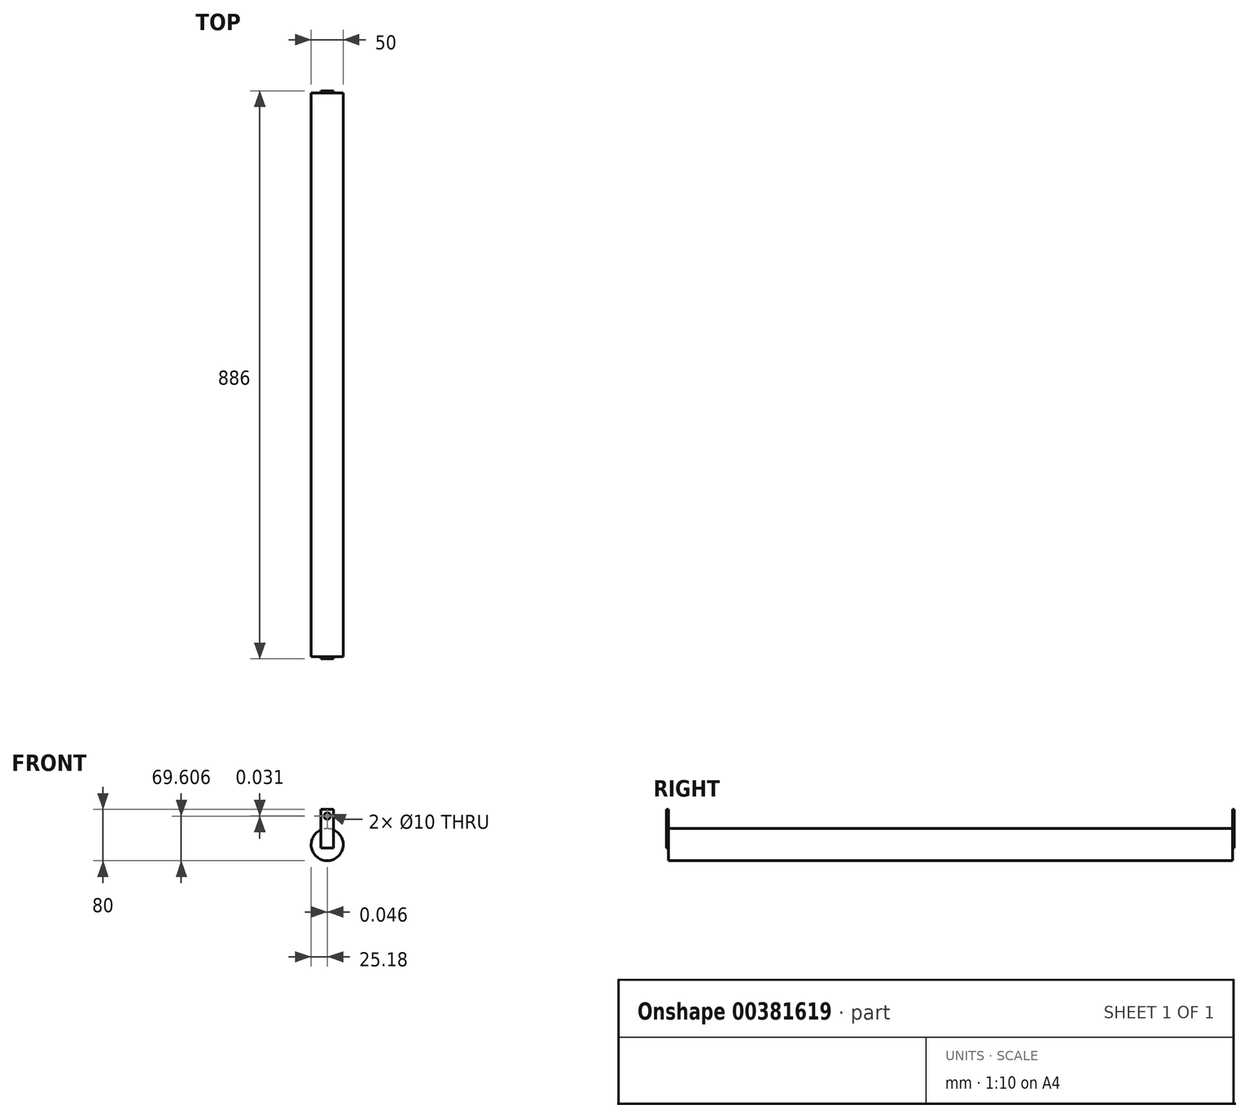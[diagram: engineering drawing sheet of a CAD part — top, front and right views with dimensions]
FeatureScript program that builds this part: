
annotation { "Feature Type Name" : "Feature", "Feature Type Description" : "" }
export const myFeature = defineFeature(function(context is Context, id is Id, definition is map)
    precondition{}
    {
        {
            var Q0;
            Q0=qCreatedBy(makeId("Front.planeOp"),FACE);
            var sketch = newSketch(context, id + "F0", { "sketchPlane" : qUnion([Q0])});
            skCircle(sketch, "E0", {"center": v(0, 0) * mm, "radius": 25 * mm});
            skLineSegment(sketch, "E1", {"start": v(-44.66, 25) * mm, "end": v(49.89, 25) * mm, "construction": true});
            skSolve(sketch);
        }
        {
            var Q0;
            Q0=makeQuery(id+"F0.imprint","IMPRINT",FACE,{"disambiguationData":[TD([[makeQuery(id+"F0.imprint","IMPRINT",EDGE,{"derivedFrom":sQuery(id+"F0.wireOp",EDGE,"E0")}),1.0]])]});
            extrude(context, id + "F1", {"entities" : qUnion([Q0]), "depth" : 880 * mm});
        }
        {
            var Q0;
            Q0=makeQuery(id+"F1.opExtrude","CAP_FACE",FACE,{"disambiguationData":[OSD([sQuery(id+"F0.wireOp",EDGE,"E0")])],"isStart":false});
            var sketch = newSketch(context, id + "F2", { "sketchPlane" : qUnion([Q0])});
            skLineSegment(sketch, "E2.bottom", {"start": v(-10, 55) * mm, "end": v(10, 55) * mm});
            skLineSegment(sketch, "E2.top", {"start": v(-10, -5) * mm, "end": v(10, -5) * mm});
            skLineSegment(sketch, "E2.left", {"start": v(-10, 55) * mm, "end": v(-10, -5) * mm});
            skLineSegment(sketch, "E2.right", {"start": v(10, 55) * mm, "end": v(10, -5) * mm});
            skCircle(sketch, "E3", {"center": v(0.23, 44.6) * mm, "radius": 5 * mm});
            skSolve(sketch);
        }
        {
            var Q0;
            {var subQ0=sQuery(id+"F2.wireOp",EDGE,"E2.bottom");Q0=makeQuery(id+"F2.imprint","IMPRINT",FACE,{"disambiguationData":[TD([[makeQuery(id+"F2.imprint","IMPRINT",EDGE,{"derivedFrom":subQ0}),-1.0]])]});}
            var Q1;
            {var subQ0=sQuery(id+"F2.wireOp",EDGE,"E2.top");Q1=makeQuery(id+"F2.imprint","IMPRINT",FACE,{"disambiguationData":[TD([[makeQuery(id+"F2.imprint","IMPRINT",EDGE,{"derivedFrom":subQ0}),1.0]])]});}
            extrude(context, id + "F3", {"entities" : qUnion([Q0, Q1]), "operationType" : NewBodyOperationType.ADD, "depth" : 3 * mm});
        }
        {
            var Q0;
            Q0=makeQuery(id+"F1.opExtrude","CAP_FACE",FACE,{"disambiguationData":[OSD([sQuery(id+"F0.wireOp",EDGE,"E0")])],"isStart":true});
            var sketch = newSketch(context, id + "F4", { "sketchPlane" : qUnion([Q0])});
            skLineSegment(sketch, "E4.bottom", {"start": v(-10, 55) * mm, "end": v(10, 55) * mm});
            skLineSegment(sketch, "E4.top", {"start": v(-10, -5) * mm, "end": v(10, -5) * mm});
            skLineSegment(sketch, "E4.left", {"start": v(-10, 55) * mm, "end": v(-10, -5) * mm});
            skLineSegment(sketch, "E4.right", {"start": v(10, 55) * mm, "end": v(10, -5) * mm});
            skCircle(sketch, "E5", {"center": v(-0.18, 44.64) * mm, "radius": 5 * mm});
            skSolve(sketch);
        }
        {
            var Q0;
            {var subQ0=sQuery(id+"F4.wireOp",EDGE,"E4.top");Q0=makeQuery(id+"F4.imprint","IMPRINT",FACE,{"disambiguationData":[TD([[makeQuery(id+"F4.imprint","IMPRINT",EDGE,{"derivedFrom":subQ0}),1.0]])]});}
            var Q1;
            {var subQ1=sQuery(id+"F4.wireOp",EDGE,"E4.bottom");Q1=makeQuery(id+"F4.imprint","IMPRINT",FACE,{"disambiguationData":[TD([[makeQuery(id+"F4.imprint","IMPRINT",EDGE,{"derivedFrom":subQ1}),-1.0]])]});}
            extrude(context, id + "F5", {"entities" : qUnion([Q0, Q1]), "operationType" : NewBodyOperationType.ADD, "depth" : 3 * mm});
        }
    });
